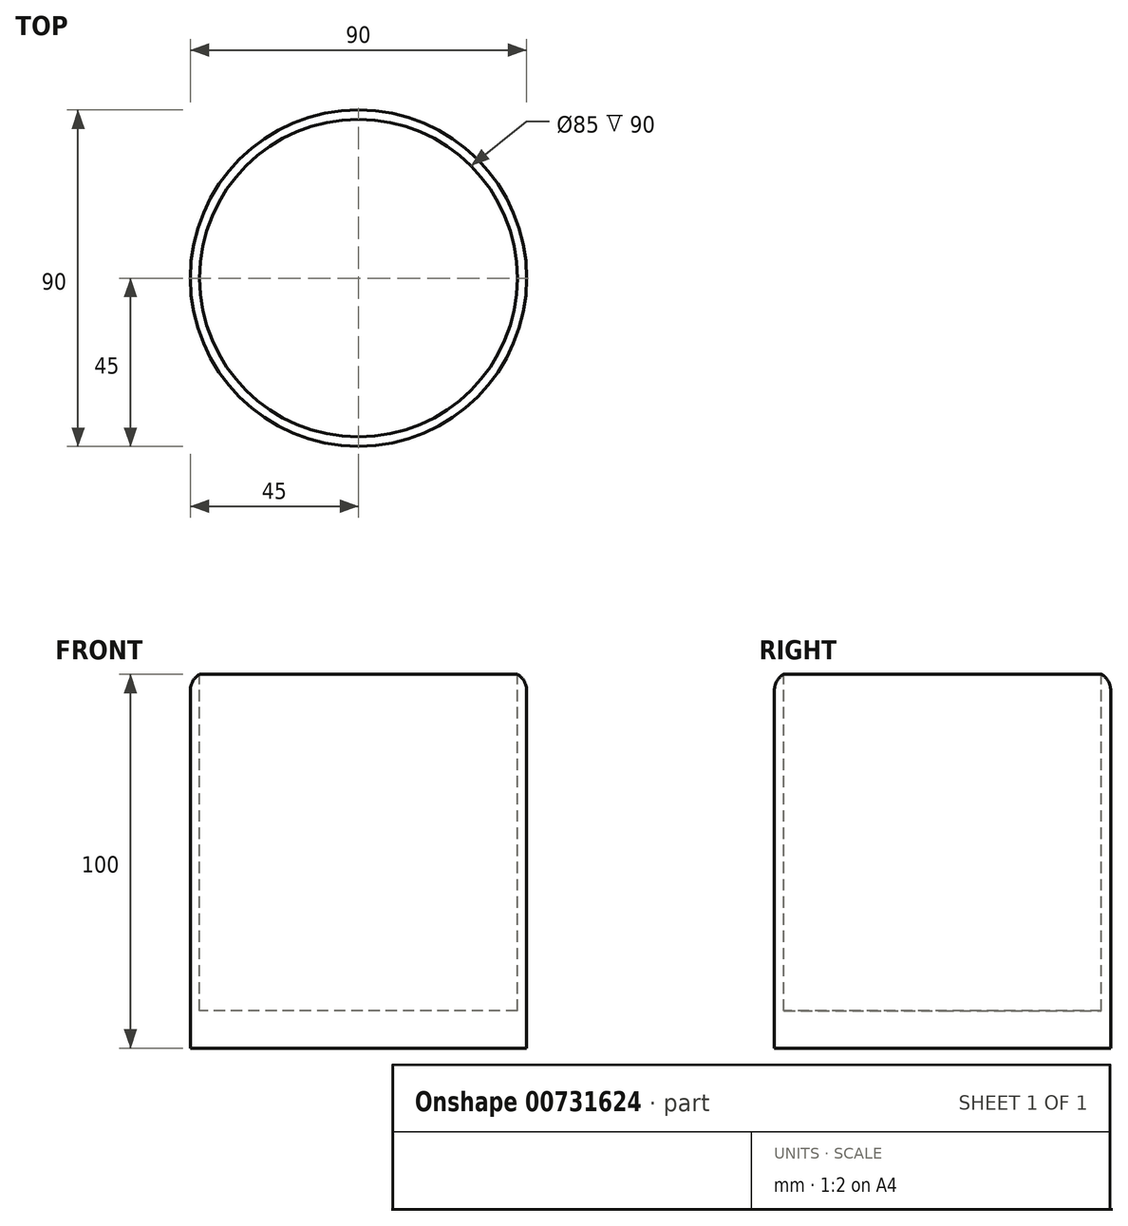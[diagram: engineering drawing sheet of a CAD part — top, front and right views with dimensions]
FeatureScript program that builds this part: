
annotation { "Feature Type Name" : "Feature", "Feature Type Description" : "" }
export const myFeature = defineFeature(function(context is Context, id is Id, definition is map)
    precondition{}
    {
        {
            var Q0;
            Q0=qCreatedBy(makeId("Top.planeOp"),FACE);
            var sketch = newSketch(context, id + "F0", { "sketchPlane" : qUnion([Q0])});
            skCircle(sketch, "E0", {"center": v(0, 0) * mm, "radius": 45 * mm});
            skSolve(sketch);
        }
        {
            var Q0;
            Q0 = qSketchRegion(id + "F0", true);
            extrude(context, id + "F1", {"entities" : qUnion([Q0]), "depth" : 100 * mm, "offsetDistance" : 25 * mm});
        }
        {
            var Q0;
            Q0=makeQuery(id+"F1.opExtrude","CAP_FACE",FACE,{"disambiguationData":[OSD([sQuery(id+"F0.wireOp",EDGE,"E0")])],"isStart":false});
            var sketch = newSketch(context, id + "F2", { "sketchPlane" : qUnion([Q0])});
            skSolve(sketch);
        }
        {
            var Q0;
            Q0=makeQuery(id+"F2.imprint","IMPRINT",FACE,{"disambiguationData":[TD([[makeQuery(id+"F2.imprint","IMPRINT",EDGE,{"derivedFrom":makeQuery(id+"F1.opExtrude","CAP_EDGE",EDGE,{"disambiguationData":[OSD([sQuery(id+"F0.wireOp",EDGE,"E0")])],"isStart":false})}),1.0]])]});
            var sketch = newSketch(context, id + "F3", { "sketchPlane" : qUnion([Q0])});
            skCircle(sketch, "E1", {"center": v(0, 0) * mm, "radius": 42.5 * mm});
            skSolve(sketch);
        }
        {
            var Q0;
            Q0 = qSketchRegion(id + "F3", true);
            extrude(context, id + "F4", {"entities" : qUnion([Q0]), "operationType" : NewBodyOperationType.REMOVE, "oppositeDirection" : true, "depth" : 90 * mm, "offsetDistance" : 25 * mm});
        }
        {
            var Q0;
            Q0=makeQuery(id+"F1.opExtrude","CAP_EDGE",EDGE,{"disambiguationData":[OSD([sQuery(id+"F0.wireOp",EDGE,"E0")])],"isStart":false});
            fillet(context, id + "F5", {"entities" : qUnion([Q0]), "radius" : 5 * mm, "tangentPropagation" : true, "allowEdgeOverflow" : false});
        }
    });
